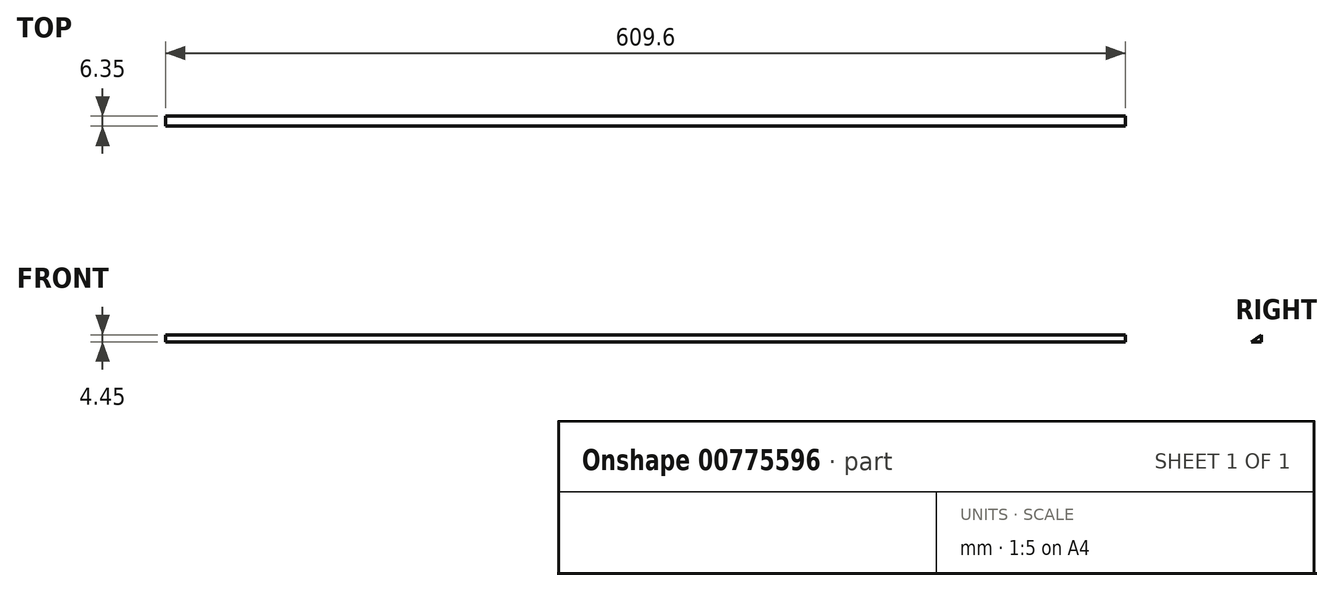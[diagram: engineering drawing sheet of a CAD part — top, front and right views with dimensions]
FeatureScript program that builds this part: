
annotation { "Feature Type Name" : "Feature", "Feature Type Description" : "" }
export const myFeature = defineFeature(function(context is Context, id is Id, definition is map)
    precondition{}
    {
        {
            var Q0;
            Q0=qCreatedBy(makeId("Right.planeOp"),FACE);
            var sketch = newSketch(context, id + "F0", { "sketchPlane" : qUnion([Q0])});
            skLineSegment(sketch, "E0", {"start": v(0, 0) * mm, "end": v(6.35, 0) * mm});
            skLineSegment(sketch, "E1", {"start": v(6.35, 0) * mm, "end": v(6.35, 4.45) * mm});
            skLineSegment(sketch, "E2", {"start": v(6.35, 4.45) * mm, "end": v(0, 0) * mm});
            skSolve(sketch);
        }
        {
            var Q0;
            Q0 = qSketchRegion(id + "F0", true);
            extrude(context, id + "F1", {"entities" : qUnion([Q0]), "endBound" : BoundingType.SYMMETRIC, "depth" : 609.6 * mm, "offsetDistance" : 25.4 * mm});
        }
    });
